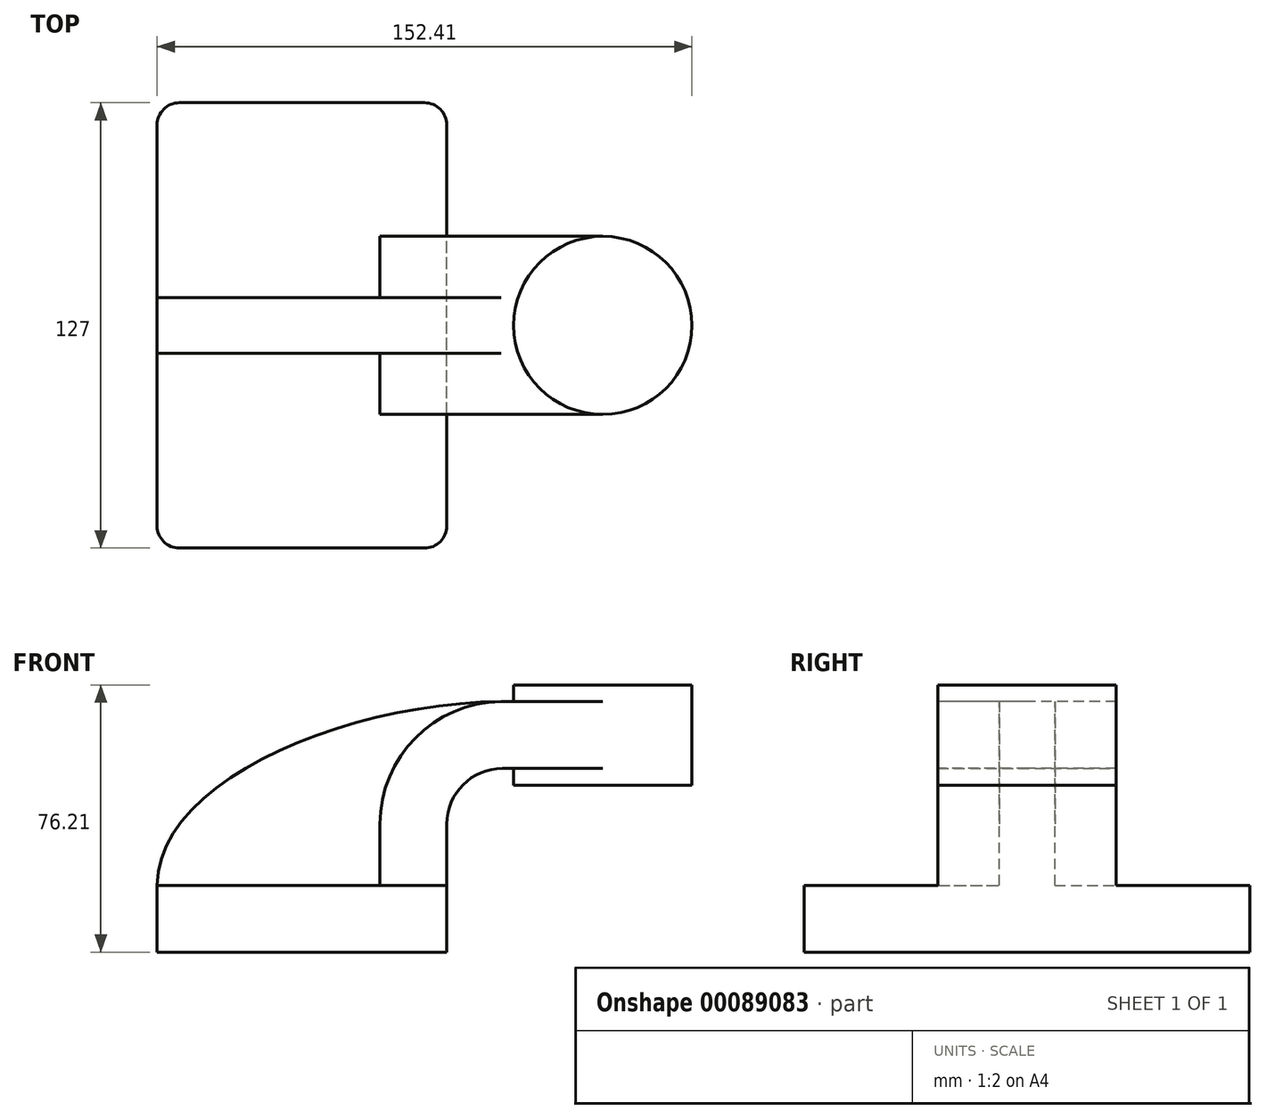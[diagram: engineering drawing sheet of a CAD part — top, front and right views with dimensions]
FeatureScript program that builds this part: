
annotation { "Feature Type Name" : "Feature", "Feature Type Description" : "" }
export const myFeature = defineFeature(function(context is Context, id is Id, definition is map)
    precondition{}
    {
        {
            var Q0;
            Q0=qCreatedBy(makeId("Front.planeOp"),FACE);
            var sketch = newSketch(context, id + "F0", { "sketchPlane" : qUnion([Q0])});
            skLineSegment(sketch, "E0.bottom", {"start": v(-41.28, -9.53) * mm, "end": v(41.28, -9.53) * mm});
            skLineSegment(sketch, "E0.top", {"start": v(-41.28, 9.53) * mm, "end": v(41.28, 9.53) * mm});
            skLineSegment(sketch, "E0.left", {"start": v(-41.28, -9.53) * mm, "end": v(-41.28, 9.53) * mm});
            skLineSegment(sketch, "E0.right", {"start": v(41.28, -9.53) * mm, "end": v(41.28, 9.52) * mm});
            skPoint(sketch, "E0.middle", {"position": v(0, 0) * mm});
            skLineSegment(sketch, "E1.bottom", {"start": v(111.13, 38.1) * mm, "end": v(60.33, 38.1) * mm});
            skLineSegment(sketch, "E1.top", {"start": v(111.13, 66.67) * mm, "end": v(60.33, 66.67) * mm});
            skLineSegment(sketch, "E1.left", {"start": v(111.13, 38.1) * mm, "end": v(111.13, 66.67) * mm});
            skLineSegment(sketch, "E1.right", {"start": v(60.33, 38.1) * mm, "end": v(60.33, 66.67) * mm});
            skPoint(sketch, "E1.middle", {"position": v(85.73, 52.39) * mm});
            skLineSegment(sketch, "E2", {"start": v(41.28, 9.52) * mm, "end": v(41.28, 26.99) * mm});
            skArc(sketch, "E3", {"start": v(41.27, 26.99) * mm, "mid": v(45.92, 38.21) * mm, "end": v(57.15, 42.86) * mm});
            skLineSegment(sketch, "E4", {"start": v(57.15, 42.86) * mm, "end": v(85.73, 42.86) * mm});
            skLineSegment(sketch, "E5.0", {"start": v(57.15, 61.91) * mm, "end": v(85.73, 61.91) * mm});
            skArc(sketch, "E5.1", {"start": v(22.22, 26.99) * mm, "mid": v(32.45, 51.68) * mm, "end": v(57.15, 61.91) * mm});
            skLineSegment(sketch, "E5.2", {"start": v(22.22, 9.52) * mm, "end": v(22.22, 26.99) * mm});
            skLineSegment(sketch, "E6", {"start": v(22.22, 9.52) * mm, "end": v(41.28, 9.53) * mm});
            skLineSegment(sketch, "E7", {"start": v(85.73, 38.1) * mm, "end": v(85.73, 66.67) * mm});
            skFitSpline(sketch, "E8", {"points": [v(-41.28, 9.53) * mm, v(57.15, 61.91) * mm], "startDerivative": vector(0.36, 89.37) * mm, "endDerivative": vector(133.51, 0.54) * mm});
            skSolve(sketch);
        }
        {
            var Q0;
            Q0=makeQuery(id+"F0.imprint","IMPRINT",FACE,{"disambiguationData":[TD([[makeQuery(id+"F0.imprint","IMPRINT",EDGE,{"derivedFrom":sQuery(id+"F0.wireOp",EDGE,"E0.bottom")}),1.0]])]});
            extrude(context, id + "F1", {"entities" : qUnion([Q0]), "endBound" : BoundingType.SYMMETRIC, "depth" : 127 * mm});
        }
        {
            var Q0;
            Q0=makeQuery(id+"F0.imprint","IMPRINT",FACE,{"disambiguationData":[TD([[makeQuery(id+"F0.imprint","IMPRINT",EDGE,{"derivedFrom":sQuery(id+"F0.wireOp",EDGE,"E2")}),1.0]])]});
            var Q1;
            {var subQ0=sQuery(id+"F0.wireOp",EDGE,"E4");var subQ1=sQuery(id+"F0.wireOp",EDGE,"E1.right");var subQ2=makeQuery(id+"F0.imprint","INTERSECT",VERTEX,{"derivedFrom":[subQ1,subQ0]});Q1=makeQuery(id+"F0.imprint","IMPRINT",FACE,{"disambiguationData":[TD([[makeQuery(id+"F0.imprint","IMPRINT",EDGE,{"disambiguationData":[TD([[subQ2,-1.0]])],"derivedFrom":subQ1}),-1.0]])]});}
            extrude(context, id + "F2", {"entities" : qUnion([Q0, Q1]), "operationType" : NewBodyOperationType.ADD, "endBound" : BoundingType.SYMMETRIC, "depth" : 50.8 * mm});
        }
        {
            var Q0;
            {var subQ0=sQuery(id+"F0.wireOp",EDGE,"E0.top");Q0=makeQuery(id+"F0.imprint","IMPRINT",FACE,{"disambiguationData":[TD([[makeQuery(id+"F0.imprint","IMPRINT",EDGE,{"derivedFrom":subQ0}),1.0]])]});}
            extrude(context, id + "F3", {"entities" : qUnion([Q0]), "operationType" : NewBodyOperationType.ADD, "endBound" : BoundingType.SYMMETRIC, "depth" : 15.88 * mm});
        }
        {
            var Q0;
            {var subQ0=sQuery(id+"F0.wireOp",EDGE,"E1.left");Q0=makeQuery(id+"F0.imprint","IMPRINT",FACE,{"disambiguationData":[TD([[makeQuery(id+"F0.imprint","IMPRINT",EDGE,{"derivedFrom":subQ0}),1.0]])]});}
            var Q1;
            Q1=sQuery(id+"F0.wireOp",EDGE,"E7");
            revolve(context, id + "F4", {"operationType" : NewBodyOperationType.ADD, "entities" : qUnion([Q0]), "axis" : qUnion([Q1]), "revolveType" : RevolveType.FULL});
        }
        {
            var Q0;
            Q0=makeQuery(id+"F1.opExtrude","CAP_EDGE",EDGE,{"disambiguationData":[OSD([sQuery(id+"F0.wireOp",EDGE,"E0.left")])],"isStart":false});
            var Q1;
            Q1=makeQuery(id+"F1.opExtrude","CAP_EDGE",EDGE,{"disambiguationData":[OSD([sQuery(id+"F0.wireOp",EDGE,"E0.right")])],"isStart":false});
            var Q2;
            Q2=makeQuery(id+"F1.opExtrude","CAP_EDGE",EDGE,{"disambiguationData":[OSD([sQuery(id+"F0.wireOp",EDGE,"E0.right")])],"isStart":true});
            var Q3;
            Q3=makeQuery(id+"F1.opExtrude","CAP_EDGE",EDGE,{"disambiguationData":[OSD([sQuery(id+"F0.wireOp",EDGE,"E0.left")])],"isStart":true});
            fillet(context, id + "F5", {"entities" : qUnion([Q0, Q1, Q2, Q3]), "radius" : 6.35 * mm, "tangentPropagation" : true, "allowEdgeOverflow" : false});
        }
    });
